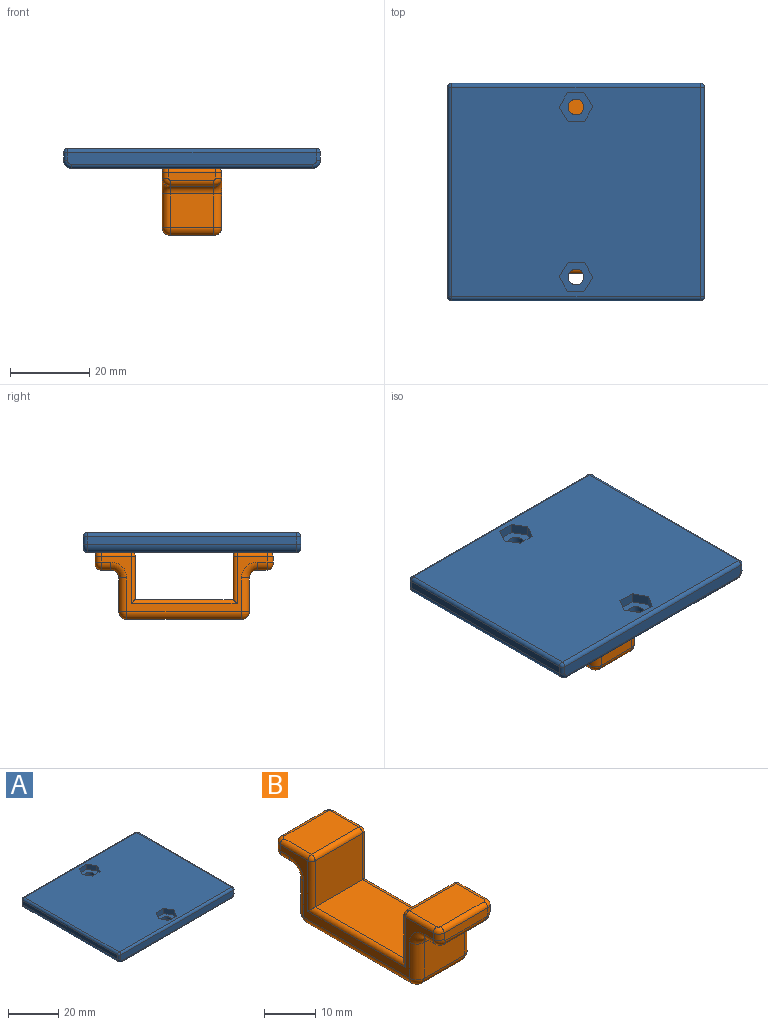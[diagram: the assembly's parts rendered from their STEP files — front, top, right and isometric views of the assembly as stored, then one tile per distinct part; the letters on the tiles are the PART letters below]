
ASSEMBLY  parts=2 mates=1
PART A: 69 faces, bbox 65.3x55x5.2 mm
  f0: plane 63x53mm, normal (0,0,1), area 3245.1mm2, adj f45,f46,f47,f48,f49,f50,f52,f53
  f1: cylinder r=2mm len=4mm, axis (0,0,1), area 18.8mm2, adj f58,f68
  f2: cylinder r=2mm len=4mm, axis (0,0,1), area 18.8mm2, adj f51,f67
  f3: plane 63x3mm, normal (0,1,0), area 188.6mm2, adj f40,f41,f42,f43,f44,f66
  f4: plane 53x2mm, normal (-1,0,0), area 106mm2, adj f17,f39,f44,f62
  f5: plane 63x3mm, normal (0,-1,0), area 188.6mm2, adj f35,f36,f37,f38,f39,f59
  f6: plane 53x2mm, normal (1,0,0), area 106mm2, adj f18,f35,f40,f63
  f7: plane 61x53mm, normal (0,0,-1), area 1891.4mm2, adj f17,f18,f19,f20,f21,f22,f23,f24
  f8: plane 46.5x1mm, normal (0,-1,0), area 46.5mm2, adj f13,f16,f19,f33
  f9: plane 23x1mm, normal (1,0,0), area 23mm2, adj f13,f14,f22,f32
  f10: plane 46.5x1mm, normal (0,1,0), area 46.5mm2, adj f14,f15,f26,f28
  f11: plane 23x1mm, normal (-1,0,0), area 23mm2, adj f15,f16,f23,f29
  f12: plane 47.5x24mm, normal (0,0,-1), area 1139.8mm2, adj f27,f28,f29,f30,f31,f32,f33,f34
  f13: cylinder r=1mm len=1mm, axis (0,0,-1), area 1.6mm2, adj f8,f9,f20,f34
  f14: cylinder r=1mm len=1mm, axis (0,0,1), area 1.6mm2, adj f9,f10,f24,f30
  f15: cylinder r=1mm len=1mm, axis (0,0,-1), area 1.6mm2, adj f10,f11,f25,f27
  f16: cylinder r=1mm len=1mm, axis (0,0,1), area 1.6mm2, adj f8,f11,f21,f31
  f17: cylinder r=2mm len=53mm, axis (0,-1,0), area 166.5mm2, adj f4,f7,f38,f43
  f18: cylinder r=2mm len=53mm, axis (0,1,0), area 166.5mm2, adj f6,f7,f36,f41
  f19: cylinder r=0.5mm len=46.5mm, axis (1,0,0), area 36.5mm2, adj f7,f8,f20,f21
  f20: torus R=1.5mm, axis (0,0,1), area 1.5mm2, adj f7,f13,f19,f22
  f21: torus R=1.5mm, axis (0,0,1), area 1.5mm2, adj f7,f16,f19,f23
  f22: cylinder r=0.5mm len=23mm, axis (0,1,0), area 18.1mm2, adj f7,f9,f20,f24
  f23: cylinder r=0.5mm len=23mm, axis (0,-1,0), area 18.1mm2, adj f7,f11,f21,f25
  f24: torus R=1.5mm, axis (0,0,1), area 1.5mm2, adj f7,f14,f22,f26
  f25: torus R=1.5mm, axis (0,0,1), area 1.5mm2, adj f7,f15,f23,f26
  f26: cylinder r=0.5mm len=46.5mm, axis (-1,0,0), area 36.5mm2, adj f7,f10,f24,f25
  f27: torus R=0.5mm, axis (0,0,1), area 1mm2, adj f12,f15,f28,f29
  f28: cylinder r=0.5mm len=46.5mm, axis (1,0,0), area 36.5mm2, adj f10,f12,f27,f30
  f29: cylinder r=0.5mm len=23mm, axis (0,1,0), area 18.1mm2, adj f11,f12,f27,f31
  f30: torus R=0.5mm, axis (0,0,1), area 1mm2, adj f12,f14,f28,f32
  f31: torus R=0.5mm, axis (0,0,1), area 1mm2, adj f12,f16,f29,f33
  f32: cylinder r=0.5mm len=23mm, axis (0,-1,0), area 18.1mm2, adj f9,f12,f30,f34
  f33: cylinder r=0.5mm len=46.5mm, axis (-1,0,0), area 36.5mm2, adj f8,f12,f31,f34
  f34: torus R=0.5mm, axis (0,0,1), area 1mm2, adj f12,f13,f32,f33
  f35: cylinder r=1mm len=2mm, axis (0,0,1), area 3.1mm2, adj f5,f6,f36,f61
  f36: torus R=1mm, axis (0,1,0), area 4mm2, adj f5,f18,f35,f37
  f37: cylinder r=1mm len=61mm, axis (1,0,0), area 95.8mm2, adj f5,f7,f36,f38
  f38: torus R=1mm, axis (0,1,0), area 4mm2, adj f5,f17,f37,f39
  f39: cylinder r=1mm len=2mm, axis (0,0,-1), area 3.1mm2, adj f4,f5,f38,f60
  f40: cylinder r=1mm len=2mm, axis (0,0,-1), area 3.1mm2, adj f3,f6,f41,f65
  f41: torus R=1mm, axis (0,1,0), area 4mm2, adj f3,f18,f40,f42
  f42: cylinder r=1mm len=61mm, axis (-1,0,0), area 95.8mm2, adj f3,f7,f41,f43
  f43: torus R=1mm, axis (0,1,0), area 4mm2, adj f3,f17,f42,f44
  f44: cylinder r=1mm len=2mm, axis (0,0,1), area 3.1mm2, adj f3,f4,f43,f64
  f45: plane 4.25x2.5mm, normal (-0.03,-1,0), area 10.6mm2, adj f0,f46,f50,f51
  f46: plane 3.62x2.5mm, normal (0.85,-0.53,0), area 10.6mm2, adj f0,f45,f47,f51
  f47: plane 3.74x2.5mm, normal (0.88,0.47,0), area 10.6mm2, adj f0,f46,f48,f51
  f48: plane 4.25x2.5mm, normal (0.03,1,0), area 10.6mm2, adj f0,f47,f49,f51
  f49: plane 3.62x2.5mm, normal (-0.85,0.53,0), area 10.6mm2, adj f0,f48,f50,f51
  f50: plane 3.74x2.5mm, normal (-0.88,-0.47,0), area 10.6mm2, adj f0,f45,f49,f51
  f51: plane 8.5x7.49mm, normal (0,0,1), area 34.4mm2, adj f2,f45,f46,f47,f48,f49,f50
  f52: plane 3.74x2.5mm, normal (0.88,-0.47,0), area 10.6mm2, adj f0,f53,f57,f58
  f53: plane 3.62x2.5mm, normal (0.85,0.53,0), area 10.6mm2, adj f0,f52,f54,f58
  f54: plane 4.25x2.5mm, normal (-0.03,1,0), area 10.6mm2, adj f0,f53,f55,f58
  f55: plane 3.74x2.5mm, normal (-0.88,0.47,0), area 10.6mm2, adj f0,f54,f56,f58
  f56: plane 3.62x2.5mm, normal (-0.85,-0.53,0), area 10.6mm2, adj f0,f55,f57,f58
  f57: plane 4.25x2.5mm, normal (0.03,-1,0), area 10.6mm2, adj f0,f52,f56,f58
  f58: plane 8.5x7.48mm, normal (0,0,1), area 34.4mm2, adj f1,f52,f53,f54,f55,f56,f57
  f59: cylinder r=1mm len=63mm, axis (-1,0,0), area 99mm2, adj f0,f5,f60,f61
  f60: sphere r=1mm, area 1.6mm2, adj f39,f59,f62
  f61: sphere r=1mm, area 1.6mm2, adj f35,f59,f63
  f62: cylinder r=1mm len=53mm, axis (0,1,0), area 83.3mm2, adj f0,f4,f60,f64
  f63: cylinder r=1mm len=53mm, axis (0,-1,0), area 83.3mm2, adj f0,f6,f61,f65
  f64: sphere r=1mm, area 1.6mm2, adj f44,f62,f66
  f65: sphere r=1mm, area 1.6mm2, adj f40,f63,f66
  f66: cylinder r=1mm len=63mm, axis (1,0,0), area 99mm2, adj f0,f3,f64,f65
  f67: torus R=3mm, axis (0,0,1), area 23.3mm2, adj f2,f7
  f68: torus R=3mm, axis (0,0,1), area 23.3mm2, adj f1,f7
PART B: 68 faces, bbox 15x45x17 mm
  f0: plane 12x2mm, normal (0,1,0), area 23.9mm2, adj f30,f31,f32,f33,f34,f59
  f1: plane 13x8.1mm, normal (0,0,1), area 105.2mm2, adj f52,f55,f56,f57,f58,f59
  f2: plane 13x11mm, normal (0,-1,0), area 143mm2, adj f3,f46,f49,f52
  f3: plane 24.8x13mm, normal (0,0,1), area 322.4mm2, adj f2,f4,f47,f50
  f4: plane 13x11mm, normal (0,1,0), area 143mm2, adj f3,f48,f51,f67
  f5: plane 13x8.1mm, normal (0,0,1), area 105.2mm2, adj f60,f61,f62,f63,f64,f67
  f6: plane 12x2mm, normal (0,-1,0), area 23.9mm2, adj f35,f36,f37,f38,f39,f60
  f7: plane 11x2.5mm, normal (0,0,-1), area 27.5mm2, adj f15,f19,f21,f37
  f8: plane 11x8.5mm, normal (0,-1,0), area 93.5mm2, adj f14,f16,f18,f19
  f9: plane 29x11mm, normal (0,0,-1), area 319mm2, adj f16,f25,f41,f44
  f10: plane 11x8.5mm, normal (0,1,0), area 93.5mm2, adj f23,f25,f26,f27
  f11: plane 11x2.5mm, normal (0,0,-1), area 27.5mm2, adj f22,f26,f29,f32
  f12: plane 42x14mm, normal (1,0,0), area 110.8mm2, adj f18,f20,f21,f27,f28,f29,f34,f39
  f13: plane 42x14mm, normal (-1,0,0), area 110.8mm2, adj f14,f15,f17,f22,f23,f24,f30,f35
  f14: cylinder r=2mm len=8.5mm, axis (0,0,-1), area 26.7mm2, adj f8,f13,f17,f40
  f15: cylinder r=2mm len=2.5mm, axis (0,1,0), area 7.9mm2, adj f7,f13,f17,f36
  f16: cylinder r=2mm len=11mm, axis (-1,0,0), area 34.6mm2, adj f8,f9,f40,f43
  f17: torus R=4mm, axis (1,0,0), area 13.5mm2, adj f13,f14,f15,f19
  f18: cylinder r=2mm len=8.5mm, axis (0,0,1), area 26.7mm2, adj f8,f12,f20,f43
  f19: cylinder r=2mm len=11mm, axis (-1,0,0), area 34.6mm2, adj f7,f8,f17,f20
  f20: torus R=4mm, axis (1,0,0), area 13.5mm2, adj f12,f18,f19,f21
  f21: cylinder r=2mm len=2.5mm, axis (0,-1,0), area 7.9mm2, adj f7,f12,f20,f38
  f22: cylinder r=2mm len=2.5mm, axis (0,1,0), area 7.9mm2, adj f11,f13,f24,f31
  f23: cylinder r=2mm len=8.5mm, axis (0,0,1), area 26.7mm2, adj f10,f13,f24,f42
  f24: torus R=4mm, axis (1,0,0), area 13.5mm2, adj f13,f22,f23,f26
  f25: cylinder r=2mm len=11mm, axis (1,0,0), area 34.6mm2, adj f9,f10,f42,f45
  f26: cylinder r=2mm len=11mm, axis (-1,0,0), area 34.6mm2, adj f10,f11,f24,f28
  f27: cylinder r=2mm len=8.5mm, axis (0,0,-1), area 26.7mm2, adj f10,f12,f28,f45
  f28: torus R=4mm, axis (1,0,0), area 13.5mm2, adj f12,f26,f27,f29
  f29: cylinder r=2mm len=2.5mm, axis (0,-1,0), area 7.9mm2, adj f11,f12,f28,f33
  f30: cylinder r=1.5mm len=1.5mm, axis (0,0,1), area 3.5mm2, adj f0,f13,f31,f58
  f31: torus R=0.5mm, axis (0,1,0), area 5.4mm2, adj f0,f22,f30,f32
  f32: cylinder r=1.5mm len=11mm, axis (-1,0,0), area 25.9mm2, adj f0,f11,f31,f33
  f33: torus R=0.5mm, axis (0,1,0), area 5.4mm2, adj f0,f29,f32,f34
  f34: cylinder r=1.5mm len=1.5mm, axis (0,0,-1), area 3.5mm2, adj f0,f12,f33,f57
  f35: cylinder r=1.5mm len=1.5mm, axis (0,0,-1), area 3.5mm2, adj f6,f13,f36,f62
  f36: torus R=0.5mm, axis (0,1,0), area 5.4mm2, adj f6,f15,f35,f37
  f37: cylinder r=1.5mm len=11mm, axis (-1,0,0), area 25.9mm2, adj f6,f7,f36,f38
  f38: torus R=0.5mm, axis (0,1,0), area 5.4mm2, adj f6,f21,f37,f39
  f39: cylinder r=1.5mm len=1.5mm, axis (0,0,1), area 3.5mm2, adj f6,f12,f38,f61
  f40: sphere r=2mm, area 6.3mm2, adj f14,f16,f41
  f41: cylinder r=2mm len=29mm, axis (0,1,0), area 91.1mm2, adj f9,f13,f40,f42
  f42: sphere r=2mm, area 6.3mm2, adj f23,f25,f41
  f43: sphere r=2mm, area 6.3mm2, adj f16,f18,f44
  f44: cylinder r=2mm len=29mm, axis (0,-1,0), area 91.1mm2, adj f9,f12,f43,f45
  f45: sphere r=2mm, area 6.3mm2, adj f25,f27,f44
  f46: cylinder r=1mm len=12mm, axis (0,0,-1), area 17.8mm2, adj f2,f13,f47,f54
  f47: cylinder r=1mm len=26.8mm, axis (0,-1,0), area 40.1mm2, adj f3,f13,f46,f48
  f48: cylinder r=1mm len=12mm, axis (0,0,1), area 17.8mm2, adj f4,f13,f47,f66
  f49: cylinder r=1mm len=12mm, axis (0,0,1), area 17.8mm2, adj f2,f12,f50,f53
  f50: cylinder r=1mm len=26.8mm, axis (0,1,0), area 40.1mm2, adj f3,f12,f49,f51
  f51: cylinder r=1mm len=12mm, axis (0,0,-1), area 17.8mm2, adj f4,f12,f50,f65
  f52: cylinder r=1mm len=13mm, axis (-1,0,0), area 20.4mm2, adj f1,f2,f53,f54
  f53: sphere r=1mm, area 1.6mm2, adj f49,f52,f55
  f54: sphere r=1mm, area 1.6mm2, adj f46,f52,f56
  f55: cylinder r=1mm len=7.6mm, axis (0,1,0), area 11.9mm2, adj f1,f12,f53,f57
  f56: cylinder r=1mm len=7.6mm, axis (0,-1,0), area 11.9mm2, adj f1,f13,f54,f58
  f57: torus R=0.5mm, axis (0,0,-1), area 2.8mm2, adj f1,f34,f55,f59
  f58: torus R=0.5mm, axis (0,0,-1), area 2.8mm2, adj f1,f30,f56,f59
  f59: cylinder r=1mm len=12mm, axis (1,0,0), area 18.8mm2, adj f0,f1,f57,f58
  f60: cylinder r=1mm len=12mm, axis (-1,0,0), area 18.8mm2, adj f5,f6,f61,f62
  f61: torus R=0.5mm, axis (0,0,-1), area 2.8mm2, adj f5,f39,f60,f63
  f62: torus R=0.5mm, axis (0,0,-1), area 2.8mm2, adj f5,f35,f60,f64
  f63: cylinder r=1mm len=7.6mm, axis (0,1,0), area 11.9mm2, adj f5,f12,f61,f65
  f64: cylinder r=1mm len=7.6mm, axis (0,-1,0), area 11.9mm2, adj f5,f13,f62,f66
  f65: sphere r=1mm, area 1.6mm2, adj f51,f63,f67
  f66: sphere r=1mm, area 1.6mm2, adj f48,f64,f67
  f67: cylinder r=1mm len=13mm, axis (1,0,0), area 20.4mm2, adj f4,f5,f65,f66
PLACE A rot(axis=(0.04,-0.07,-1),0deg) t=(4.21,-72.36,-27.22)mm
PLACE B rot(axis=(0.04,-0.07,-1),0deg) t=(-3.31,-70.36,-27.22)mm
MATE planar A.f7 <-> B.f5  axis (0,0,-1) through (4.21,-72.36,-27.22)mm
